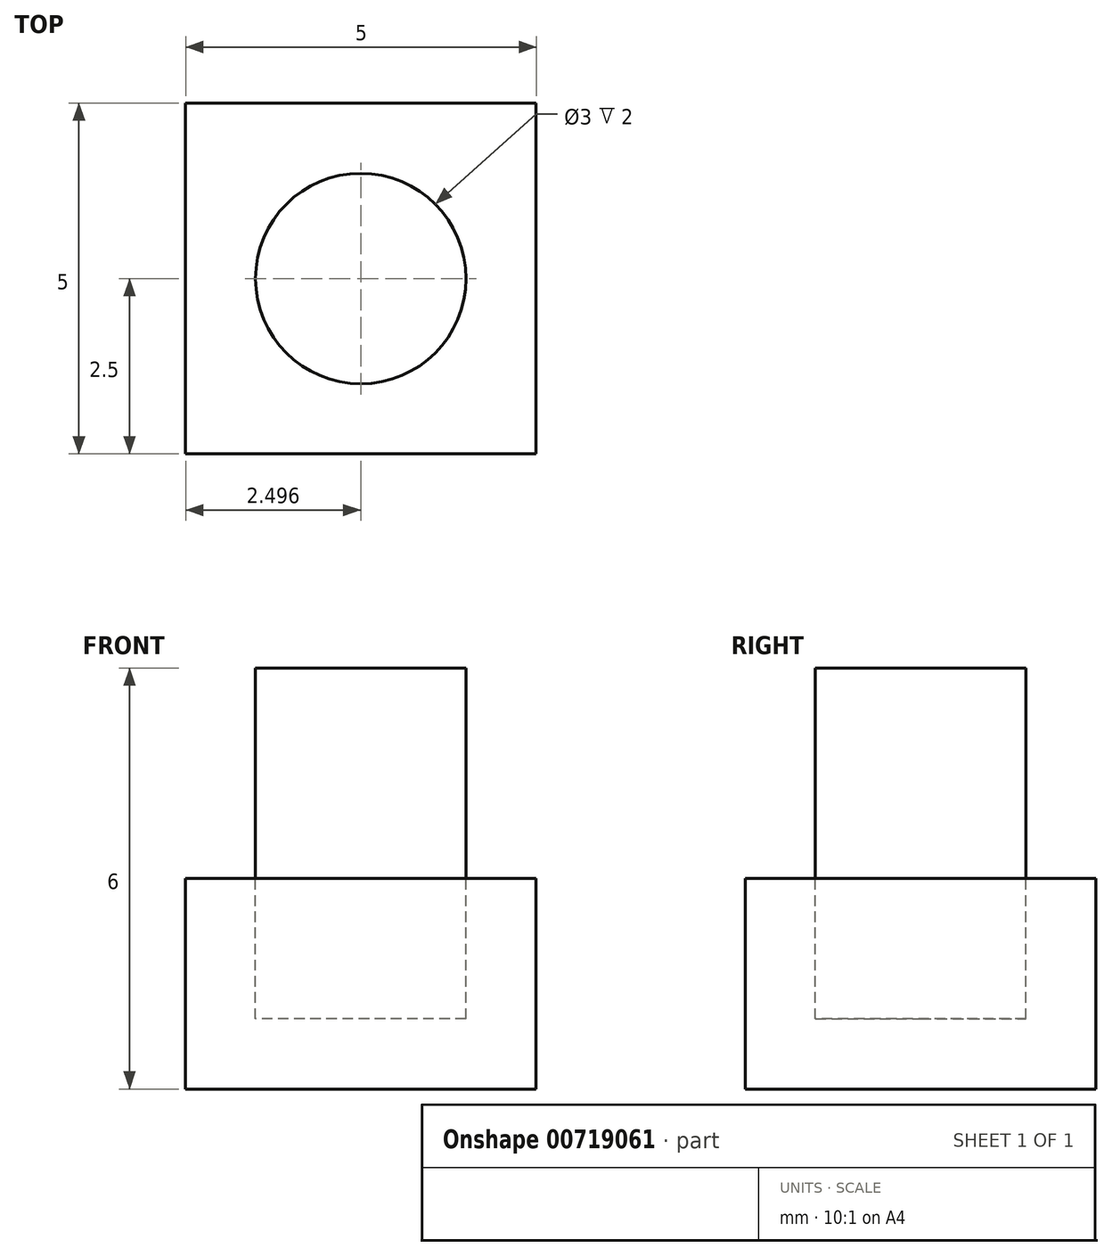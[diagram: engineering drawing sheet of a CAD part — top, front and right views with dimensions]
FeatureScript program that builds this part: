
annotation { "Feature Type Name" : "Feature", "Feature Type Description" : "" }
export const myFeature = defineFeature(function(context is Context, id is Id, definition is map)
    precondition{}
    {
        {
            var Q0;
            Q0=qCreatedBy(makeId("Top.planeOp"),FACE);
            var sketch = newSketch(context, id + "F0", { "sketchPlane" : qUnion([Q0])});
            skLineSegment(sketch, "E0.bottom", {"start": v(-2.04, 2.24) * mm, "end": v(2.96, 2.24) * mm});
            skLineSegment(sketch, "E0.top", {"start": v(-2.04, -2.76) * mm, "end": v(2.96, -2.76) * mm});
            skLineSegment(sketch, "E0.left", {"start": v(-2.04, 2.24) * mm, "end": v(-2.04, -2.76) * mm});
            skLineSegment(sketch, "E0.right", {"start": v(2.96, 2.24) * mm, "end": v(2.96, -2.76) * mm});
            skSolve(sketch);
        }
        {
            var Q0;
            Q0=makeQuery(id+"F0.imprint","IMPRINT",FACE,{"disambiguationData":[TD([[makeQuery(id+"F0.imprint","IMPRINT",EDGE,{"derivedFrom":sQuery(id+"F0.wireOp",EDGE,"E0.bottom")}),-1.0]])]});
            extrude(context, id + "F1", {"entities" : qUnion([Q0]), "depth" : 3 * mm, "offsetDistance" : 25 * mm});
        }
        {
            var Q0;
            Q0=makeQuery(id+"F1.opExtrude","CAP_FACE",FACE,{"disambiguationData":[OSD([sQuery(id+"F0.wireOp",EDGE,"E0.bottom"),sQuery(id+"F0.wireOp",EDGE,"E0.top"),sQuery(id+"F0.wireOp",EDGE,"E0.left"),sQuery(id+"F0.wireOp",EDGE,"E0.right")])],"isStart":false});
            var sketch = newSketch(context, id + "F2", { "sketchPlane" : qUnion([Q0])});
            skCircle(sketch, "E1", {"center": v(0.46, -0.26) * mm, "radius": 1.5 * mm});
            skPoint(sketch, "E1.centerSnap0", {"position": v(0.46, -2.76) * mm});
            skPoint(sketch, "E1.centerSnap1", {"position": v(-2.04, -0.26) * mm});
            skSolve(sketch);
        }
        {
            var Q0;
            Q0=makeQuery(id+"F2.imprint","IMPRINT",FACE,{"disambiguationData":[TD([[makeQuery(id+"F2.imprint","IMPRINT",EDGE,{"derivedFrom":sQuery(id+"F2.wireOp",EDGE,"E1")}),1.0]])]});
            extrude(context, id + "F3", {"entities" : qUnion([Q0]), "operationType" : NewBodyOperationType.REMOVE, "oppositeDirection" : true, "depth" : 2 * mm, "offsetDistance" : 25 * mm});
        }
        {
            var Q0;
            Q0 = qSketchRegion(id + "F2", true);
            extrude(context, id + "F4", {"entities" : qUnion([Q0]), "depth" : 3 * mm, "offsetDistance" : 25 * mm});
        }
    });
